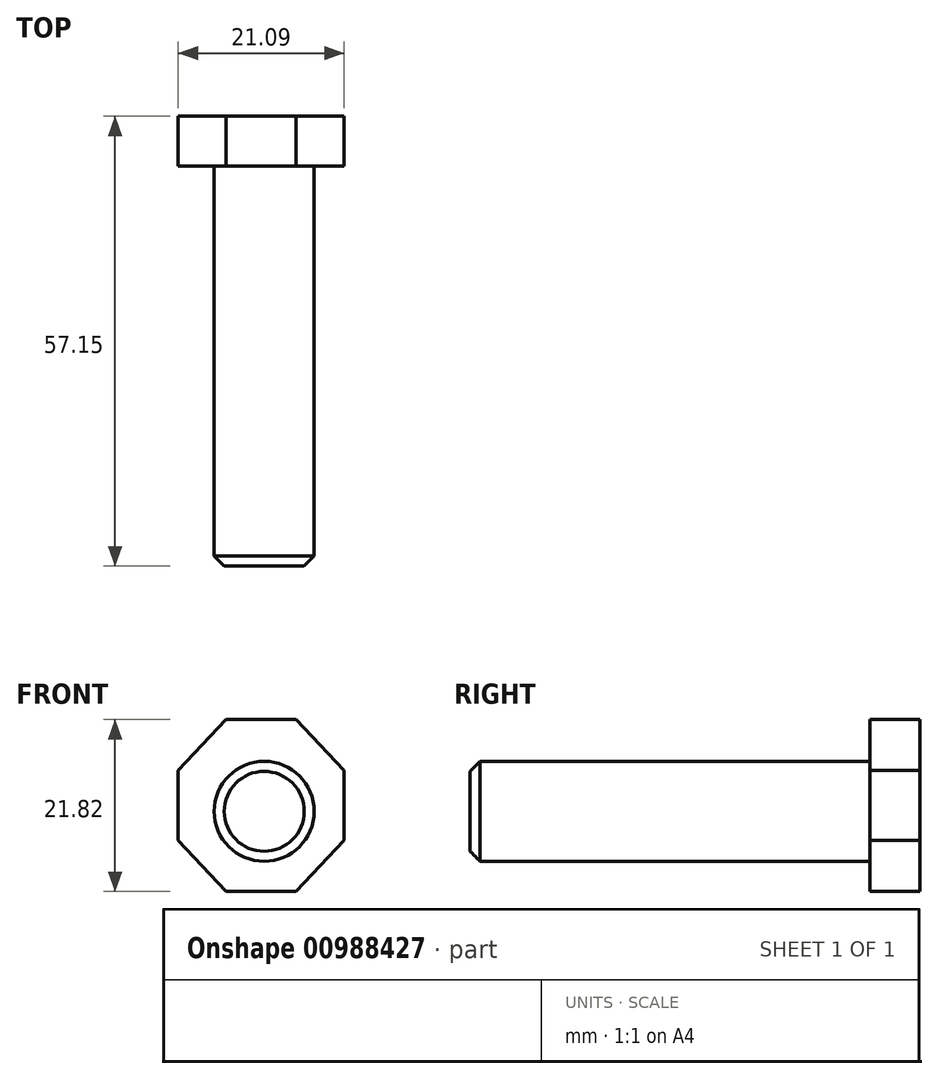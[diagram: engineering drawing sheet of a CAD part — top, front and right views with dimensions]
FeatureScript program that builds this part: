
annotation { "Feature Type Name" : "Feature", "Feature Type Description" : "" }
export const myFeature = defineFeature(function(context is Context, id is Id, definition is map)
    precondition{}
    {
        {
            var Q0;
            Q0=qCreatedBy(makeId("Front.planeOp"),FACE);
            var sketch = newSketch(context, id + "F0", { "sketchPlane" : qUnion([Q0])});
            skCircle(sketch, "E0", {"center": v(0, 0) * mm, "radius": 6.35 * mm});
            skSolve(sketch);
        }
        {
            var Q0;
            Q0=makeQuery(id+"F0.imprint","IMPRINT",FACE,{"disambiguationData":[TD([[makeQuery(id+"F0.imprint","IMPRINT",EDGE,{"derivedFrom":sQuery(id+"F0.wireOp",EDGE,"E0")}),1.0]])]});
            extrude(context, id + "F1", {"entities" : qUnion([Q0]), "depth" : 50.8 * mm, "offsetDistance" : 25.4 * mm});
        }
        {
            var Q0;
            Q0=qCreatedBy(makeId("Front.planeOp"),FACE);
            var sketch = newSketch(context, id + "F2", { "sketchPlane" : qUnion([Q0])});
            skLineSegment(sketch, "E1", {"start": v(-4.83, -10.16) * mm, "end": v(4.06, -10.16) * mm});
            skLineSegment(sketch, "E2", {"start": v(4.06, -10.16) * mm, "end": v(10.16, -3.7) * mm});
            skLineSegment(sketch, "E3", {"start": v(10.16, -3.7) * mm, "end": v(10.16, 5.2) * mm});
            skLineSegment(sketch, "E4", {"start": v(10.16, 5.2) * mm, "end": v(4.06, 11.66) * mm});
            skLineSegment(sketch, "E5", {"start": v(4.06, 11.66) * mm, "end": v(-4.83, 11.66) * mm});
            skLineSegment(sketch, "E6", {"start": v(-4.83, 11.66) * mm, "end": v(-10.93, 5.2) * mm});
            skLineSegment(sketch, "E7", {"start": v(-10.93, 5.2) * mm, "end": v(-10.93, -3.7) * mm});
            skLineSegment(sketch, "E8", {"start": v(-10.93, -3.7) * mm, "end": v(-4.83, -10.16) * mm});
            skSolve(sketch);
        }
        {
            var Q0;
            Q0=makeQuery(id+"F2.imprint","IMPRINT",FACE,{"disambiguationData":[TD([[makeQuery(id+"F2.imprint","IMPRINT",EDGE,{"derivedFrom":sQuery(id+"F2.wireOp",EDGE,"E1")}),1.0]])]});
            extrude(context, id + "F3", {"entities" : qUnion([Q0]), "operationType" : NewBodyOperationType.ADD, "oppositeDirection" : true, "depth" : 6.35 * mm, "offsetDistance" : 25.4 * mm});
        }
        {
            var Q0;
            Q0=makeQuery(id+"F1.opExtrude","CAP_EDGE",EDGE,{"disambiguationData":[OSD([sQuery(id+"F0.wireOp",EDGE,"E0")])],"isStart":false});
            chamfer(context, id + "F4", {"entities" : qUnion([Q0]), "width" : 1.27 * mm, "tangentPropagation" : true});
        }
    });
